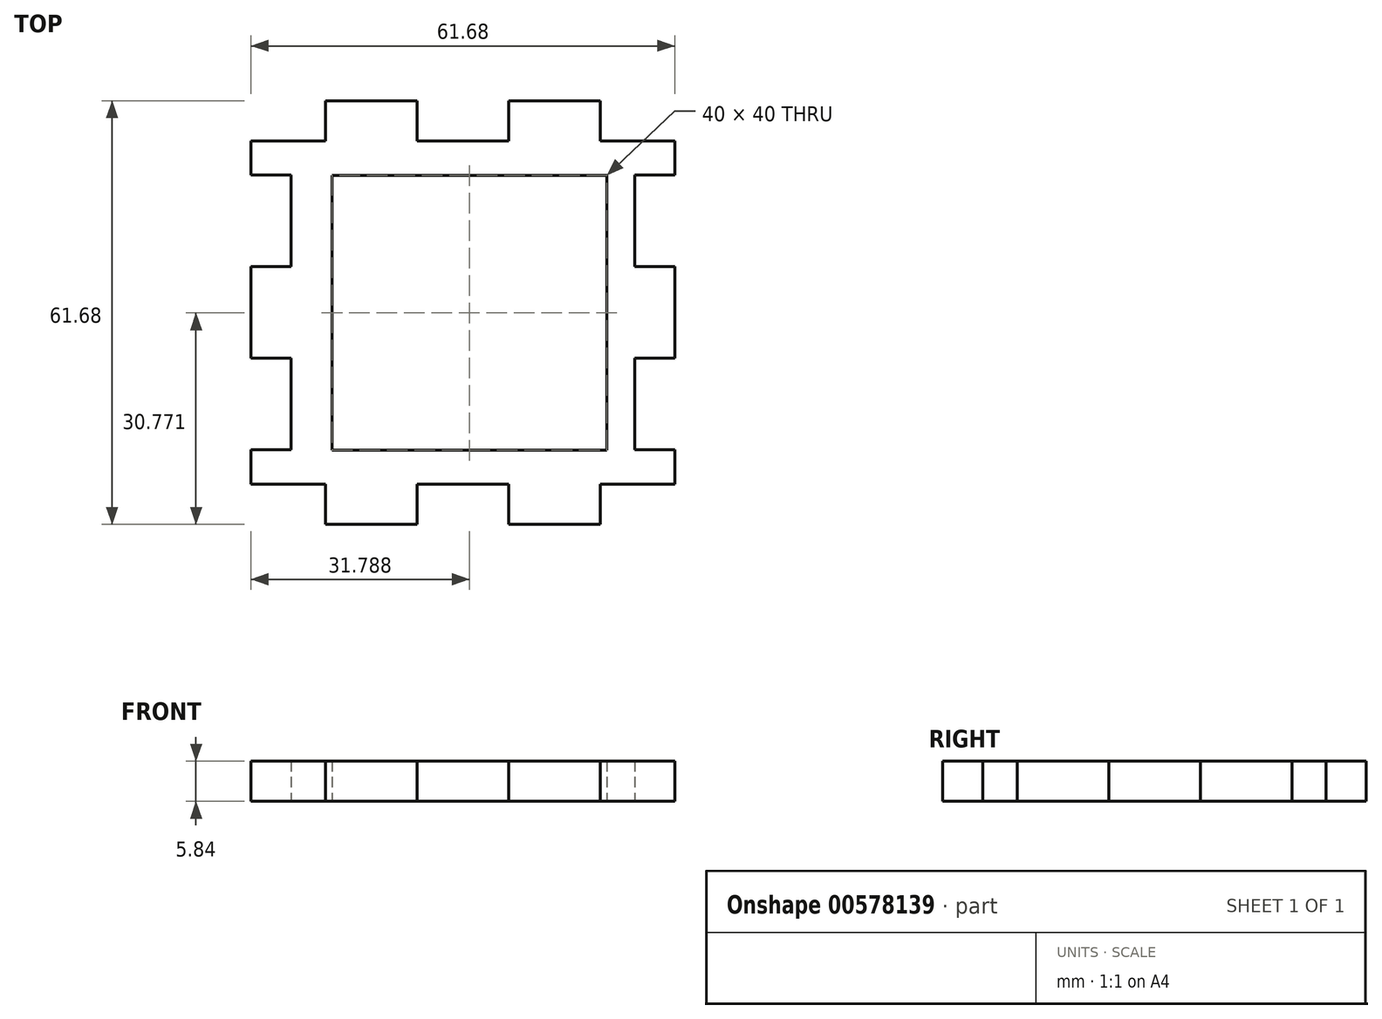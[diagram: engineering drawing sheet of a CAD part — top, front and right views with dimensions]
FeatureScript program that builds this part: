
annotation { "Feature Type Name" : "Feature", "Feature Type Description" : "" }
export const myFeature = defineFeature(function(context is Context, id is Id, definition is map)
    precondition{}
    {
        {
            var Q0;
            Q0=qCreatedBy(makeId("Top.planeOp"),FACE);
            var sketch = newSketch(context, id + "F0", { "sketchPlane" : qUnion([Q0])});
            skLineSegment(sketch, "E0.bottom", {"start": v(-25, 25) * mm, "end": v(-20, 25) * mm});
            skLineSegment(sketch, "E0.top", {"start": v(-25, -25) * mm, "end": v(-20, -25) * mm});
            skLineSegment(sketch, "E0.left", {"start": v(-25, 20) * mm, "end": v(-25, 6.67) * mm});
            skLineSegment(sketch, "E0.right", {"start": v(25, -6.67) * mm, "end": v(25, -20) * mm});
            skLineSegment(sketch, "E1", {"start": v(0, 25) * mm, "end": v(0, -25) * mm, "construction": true});
            skLineSegment(sketch, "E2", {"start": v(-25, 0) * mm, "end": v(25, 0) * mm, "construction": true});
            skLineSegment(sketch, "E3.bottom", {"start": v(-20, 30.84) * mm, "end": v(-6.67, 30.84) * mm});
            skLineSegment(sketch, "E3.top", {"start": v(-20, -30.84) * mm, "end": v(-6.67, -30.84) * mm});
            skLineSegment(sketch, "E3.left", {"start": v(-30.84, 25) * mm, "end": v(-30.84, 20) * mm});
            skLineSegment(sketch, "E3.right", {"start": v(30.84, 25) * mm, "end": v(30.84, 20) * mm});
            skLineSegment(sketch, "E4.top", {"start": v(-30.84, 25) * mm, "end": v(-20, 25) * mm});
            skLineSegment(sketch, "E4.right", {"start": v(-20, 30.84) * mm, "end": v(-20, 25) * mm});
            skLineSegment(sketch, "E5.top", {"start": v(-30.84, -25) * mm, "end": v(-20, -25) * mm});
            skLineSegment(sketch, "E5.right", {"start": v(-20, -30.84) * mm, "end": v(-20, -25) * mm});
            skLineSegment(sketch, "E6.top", {"start": v(30.84, -25) * mm, "end": v(20, -25) * mm});
            skLineSegment(sketch, "E6.right", {"start": v(20, -30.84) * mm, "end": v(20, -25) * mm});
            skLineSegment(sketch, "E7.top", {"start": v(30.84, 25) * mm, "end": v(20, 25) * mm});
            skLineSegment(sketch, "E7.right", {"start": v(20, 30.84) * mm, "end": v(20, 25) * mm});
            skLineSegment(sketch, "E8.bottom", {"start": v(-30.84, 20) * mm, "end": v(-25, 20) * mm});
            skLineSegment(sketch, "E8.top", {"start": v(-30.84, 6.67) * mm, "end": v(-25, 6.67) * mm});
            skLineSegment(sketch, "E9.bottom", {"start": v(-30.84, -6.67) * mm, "end": v(-25, -6.67) * mm});
            skLineSegment(sketch, "E9.top", {"start": v(-30.84, -20) * mm, "end": v(-25, -20) * mm});
            skLineSegment(sketch, "E9.right", {"start": v(-25, -6.67) * mm, "end": v(-25, -20) * mm});
            skLineSegment(sketch, "E10.bottom", {"start": v(25, 20) * mm, "end": v(30.84, 20) * mm});
            skLineSegment(sketch, "E10.top", {"start": v(25, 6.67) * mm, "end": v(30.84, 6.67) * mm});
            skLineSegment(sketch, "E10.left", {"start": v(25, 20) * mm, "end": v(25, 6.67) * mm});
            skLineSegment(sketch, "E11.bottom", {"start": v(25, -6.67) * mm, "end": v(30.84, -6.67) * mm});
            skLineSegment(sketch, "E11.top", {"start": v(25, -20) * mm, "end": v(30.84, -20) * mm});
            skLineSegment(sketch, "E12.top", {"start": v(-6.67, 25) * mm, "end": v(6.67, 25) * mm});
            skLineSegment(sketch, "E12.left", {"start": v(-6.67, 30.84) * mm, "end": v(-6.67, 25) * mm});
            skLineSegment(sketch, "E12.right", {"start": v(6.67, 30.84) * mm, "end": v(6.67, 25) * mm});
            skLineSegment(sketch, "E13.bottom", {"start": v(-6.67, -25) * mm, "end": v(6.67, -25) * mm});
            skLineSegment(sketch, "E13.left", {"start": v(-6.67, -25) * mm, "end": v(-6.67, -30.84) * mm});
            skLineSegment(sketch, "E13.right", {"start": v(6.67, -25) * mm, "end": v(6.67, -30.84) * mm});
            skLineSegment(sketch, "E14.trimOffspring", {"start": v(30.84, 6.67) * mm, "end": v(30.84, -6.67) * mm});
            skLineSegment(sketch, "E15.trimOffspring", {"start": v(20, 25) * mm, "end": v(25, 25) * mm});
            skLineSegment(sketch, "E16.trimOffspring", {"start": v(6.67, 30.84) * mm, "end": v(20, 30.84) * mm});
            skLineSegment(sketch, "E17.trimOffspring", {"start": v(-30.84, 6.67) * mm, "end": v(-30.84, -6.67) * mm});
            skLineSegment(sketch, "E18.trimOffspring", {"start": v(-30.84, -20) * mm, "end": v(-30.84, -25) * mm});
            skLineSegment(sketch, "E19.trimOffspring", {"start": v(6.67, -30.84) * mm, "end": v(20, -30.84) * mm});
            skLineSegment(sketch, "E20.trimOffspring", {"start": v(30.84, -20) * mm, "end": v(30.84, -25) * mm});
            skLineSegment(sketch, "E21.trimOffspring", {"start": v(20, -25) * mm, "end": v(25, -25) * mm});
            skLineSegment(sketch, "E22.bottom", {"start": v(-19.05, 19.93) * mm, "end": v(20.95, 19.93) * mm});
            skLineSegment(sketch, "E22.top", {"start": v(-19.05, -20.07) * mm, "end": v(20.95, -20.07) * mm});
            skLineSegment(sketch, "E22.left", {"start": v(-19.05, 19.93) * mm, "end": v(-19.05, -20.07) * mm});
            skLineSegment(sketch, "E22.right", {"start": v(20.95, 19.93) * mm, "end": v(20.95, -20.07) * mm});
            skSolve(sketch);
        }
        {
            var Q0;
            Q0=makeQuery(id+"F0.imprint","IMPRINT",FACE,{"disambiguationData":[TD([[makeQuery(id+"F0.imprint","IMPRINT",EDGE,{"derivedFrom":sQuery(id+"F0.wireOp",EDGE,"E3.bottom")}),-1.0]])]});
            extrude(context, id + "F1", {"entities" : qUnion([Q0]), "depth" : 5.84 * mm});
        }
    });
